# Revit family: Infire_Industrial
name_source: partatom
category: Zabudowa
revit_build: Autodesk Revit 2018 (Build: 20180329_1100(x64)
units: mm (PartAtom-declared; Revit-internal decimal feet)

## family parameters
Numer OmniClass = 23.40.20.34.14
Obiekt nadrzędny = Powierzchnia
Punkt obliczania pomieszczeń = Nie
Tnij formami wycięć po wczytaniu = Nie
Tytuł OmniClass = Fireplaces
Współdzielony = Nie

## types (1)
- INDUSTRIAL
    Domyślna rzędna = 1000 mm  [stored 3.28084 ft]
    Grubość paleniska = 140 mm  [stored 0.459318 ft]
    Gwarancja = 24 miesiące
    Głębokość = 300 mm
    IfcExportAs = IfcSpaceHeaterType
    Komentarze do typu = Biokominek
    Materiał (obudowa) = INFIRE - rdzawy
    Materiał (szkło) = INFIRE - szkło
    Materiał (wkład) = INFIRE - czarny
    Model = INDUSTRIAL
    Obraz typu = Infire_Industrial.jpg
    Producent = INFIRE Biokominki
    Szerokość = 1000 mm  [stored 3.28084 ft]
    Szerokość paleniska = 300 mm
    Szerokość szyby = 900 mm  [stored 2.95276 ft]
    Szkło = Szyba hartowana 4 mm, przyciemniana
    URL = http://www.infire.pl
    Wysokość = 470 mm  [stored 1.54199 ft]
    Wysokość szyby = 320 mm  [stored 1.04987 ft]

note: [stored X ft] marks values corroborated as IEEE doubles in the binary element streams (Revit-internal decimal feet)
